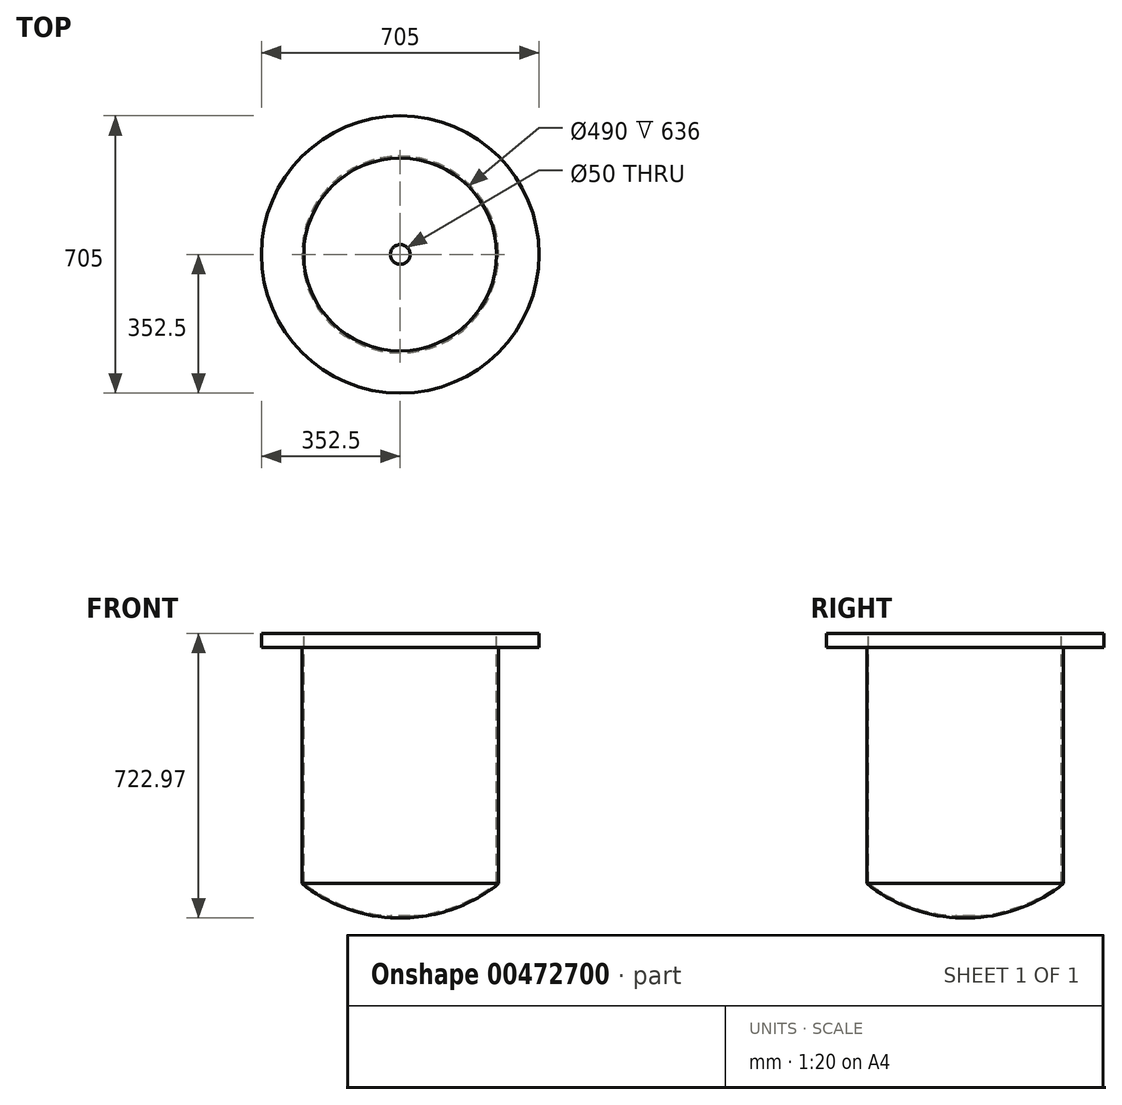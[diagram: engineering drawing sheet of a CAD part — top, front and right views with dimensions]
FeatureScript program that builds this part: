
annotation { "Feature Type Name" : "Feature", "Feature Type Description" : "" }
export const myFeature = defineFeature(function(context is Context, id is Id, definition is map)
    precondition{}
    {
        {
            var Q0;
            Q0=qCreatedBy(makeId("Front.planeOp"),FACE);
            var sketch = newSketch(context, id + "F0", { "sketchPlane" : qUnion([Q0])});
            skLineSegment(sketch, "E0", {"start": v(0, 524.77) * mm, "end": v(0, -475.23) * mm});
            skLineSegment(sketch, "E1", {"start": v(250, 0) * mm, "end": v(250, 600) * mm});
            skArc(sketch, "E2", {"start": v(0, -87.75) * mm, "mid": v(132.48, -65.18) * mm, "end": v(250, 0) * mm});
            skLineSegment(sketch, "E3", {"start": v(250, 600) * mm, "end": v(352.5, 600) * mm});
            skLineSegment(sketch, "E4", {"start": v(352.5, 600) * mm, "end": v(352.5, 636) * mm});
            skLineSegment(sketch, "E5", {"start": v(352.5, 636) * mm, "end": v(245, 636) * mm});
            skLineSegment(sketch, "E6", {"start": v(245, 636) * mm, "end": v(245, 0) * mm});
            skArc(sketch, "E7", {"start": v(0, -82.75) * mm, "mid": v(129.3, -61.5) * mm, "end": v(245, 0) * mm});
            skPoint(sketch, "E8.orphan", {"position": v(-250, 0) * mm});
            skPoint(sketch, "E9.orphan", {"position": v(-245, 0) * mm});
            skLineSegment(sketch, "E10", {"start": v(0, -82.75) * mm, "end": v(0, -87.75) * mm});
            skSolve(sketch);
        }
        {
            var Q0;
            Q0 = qSketchRegion(id + "F0", true);
            var Q1;
            Q1=sQuery(id+"F0.wireOp",EDGE,"E0");
            revolve(context, id + "F1", {"entities" : qUnion([Q0]), "axis" : qUnion([Q1]), "revolveType" : RevolveType.FULL});
        }
        {
            var Q0;
            Q0=qCreatedBy(makeId("Top.planeOp"),FACE);
            var sketch = newSketch(context, id + "F2", { "sketchPlane" : qUnion([Q0])});
            skCircle(sketch, "E11", {"center": v(0, 0) * mm, "radius": 25 * mm});
            skSolve(sketch);
        }
        {
            var Q0;
            Q0=makeQuery(id+"F2.imprint","IMPRINT",FACE,{"disambiguationData":[TD([[makeQuery(id+"F2.imprint","IMPRINT",EDGE,{"derivedFrom":sQuery(id+"F2.wireOp",EDGE,"E11")}),1.0]])]});
            extrude(context, id + "F3", {"entities" : qUnion([Q0]), "operationType" : NewBodyOperationType.REMOVE, "endBound" : BoundingType.THROUGH_ALL, "oppositeDirection" : true, "depth" : 25 * mm});
        }
    });
